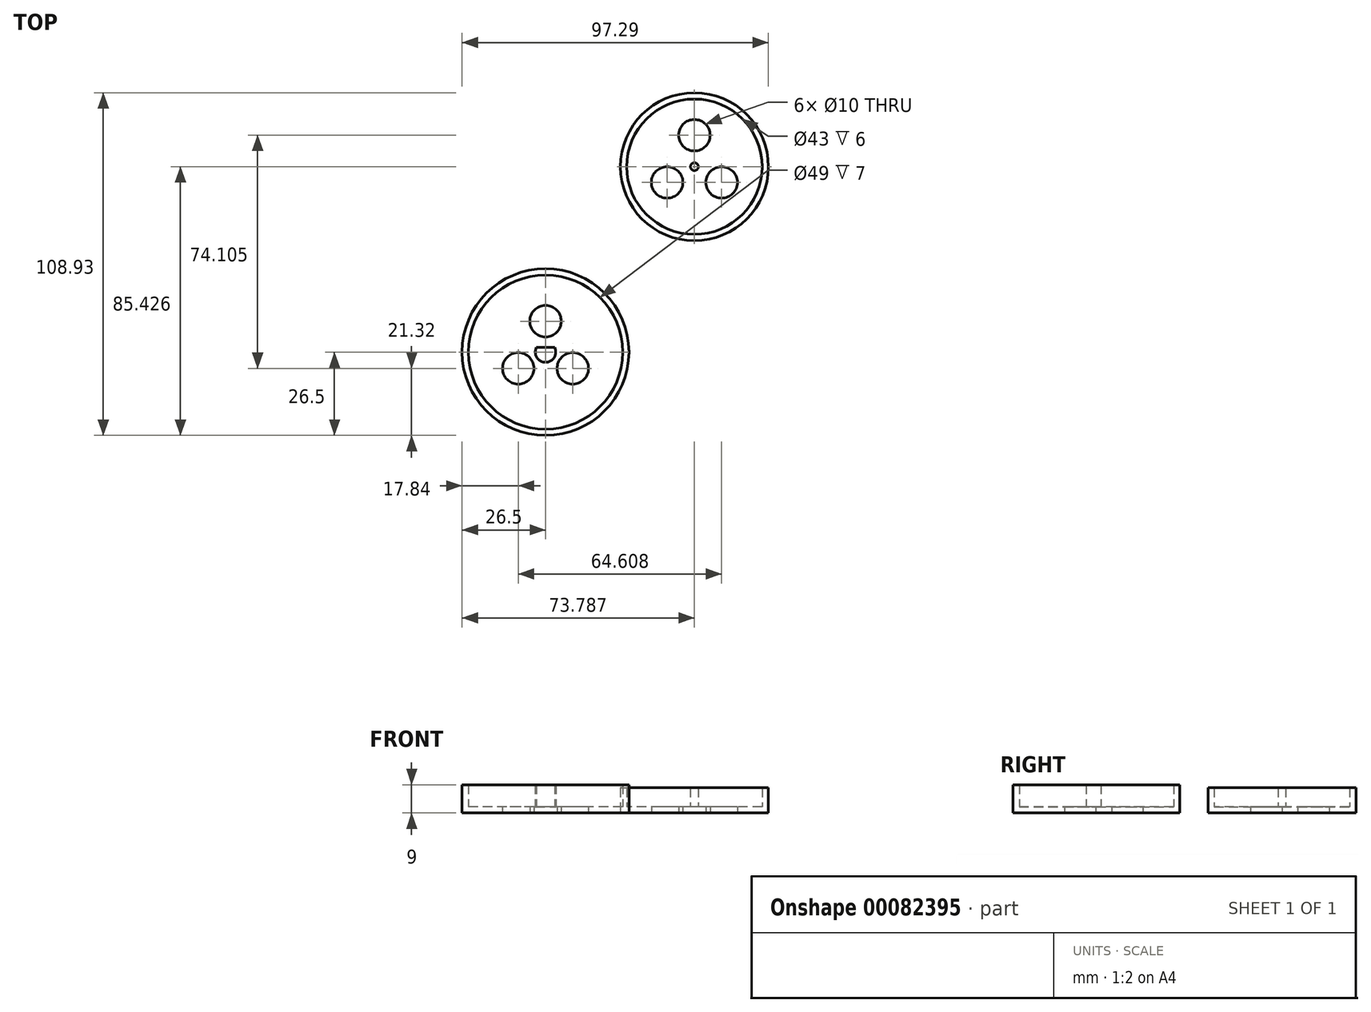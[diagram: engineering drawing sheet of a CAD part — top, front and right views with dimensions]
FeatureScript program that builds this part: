
annotation { "Feature Type Name" : "Feature", "Feature Type Description" : "" }
export const myFeature = defineFeature(function(context is Context, id is Id, definition is map)
    precondition{}
    {
        {
            var Q0;
            Q0=qCreatedBy(makeId("Top.planeOp"),FACE);
            var sketch = newSketch(context, id + "F0", { "sketchPlane" : qUnion([Q0])});
            skCircle(sketch, "E0", {"center": v(0, 0) * mm, "radius": 24.5 * mm});
            skCircle(sketch, "E1", {"center": v(0, 0) * mm, "radius": 26.5 * mm});
            skArc(sketch, "E2", {"start": v(-2.88, 1.5) * mm, "mid": v(0, -3.25) * mm, "end": v(2.88, 1.5) * mm});
            skLineSegment(sketch, "E3", {"start": v(2.88, 1.5) * mm, "end": v(-2.88, 1.5) * mm});
            skCircle(sketch, "E4", {"center": v(0, 9.82) * mm, "radius": 5 * mm});
            skCircle(sketch, "E5.1.0", {"center": v(-8.66, -5.18) * mm, "radius": 5 * mm});
            skCircle(sketch, "E5.2.0", {"center": v(8.66, -5.18) * mm, "radius": 5 * mm});
            skPoint(sketch, "E5.center", {"position": v(0, -0.18) * mm});
            skCircle(sketch, "E6", {"center": v(47.29, 58.93) * mm, "radius": 23.5 * mm});
            skCircle(sketch, "E7", {"center": v(47.29, 58.93) * mm, "radius": 21.5 * mm});
            skCircle(sketch, "E8", {"center": v(47.29, 68.93) * mm, "radius": 5 * mm});
            skCircle(sketch, "E9.1.0", {"center": v(38.63, 53.93) * mm, "radius": 5 * mm});
            skCircle(sketch, "E9.2.0", {"center": v(55.95, 53.93) * mm, "radius": 5 * mm});
            skCircle(sketch, "E10", {"center": v(47.29, 58.93) * mm, "radius": 1.25 * mm});
            skSolve(sketch);
        }
        {
            var Q0;
            Q0=makeQuery(id+"F0.imprint","IMPRINT",FACE,{"disambiguationData":[TD([[makeQuery(id+"F0.imprint","IMPRINT",EDGE,{"derivedFrom":sQuery(id+"F0.wireOp",EDGE,"E2")}),1.0]])]});
            var Q1;
            Q1=makeQuery(id+"F0.imprint","IMPRINT",FACE,{"disambiguationData":[TD([[makeQuery(id+"F0.imprint","IMPRINT",EDGE,{"derivedFrom":sQuery(id+"F0.wireOp",EDGE,"E0")}),-1.0]])]});
            extrude(context, id + "F1", {"entities" : qUnion([Q0, Q1]), "depth" : 9 * mm});
        }
        {
            var Q0;
            Q0=makeQuery(id+"F0.imprint","IMPRINT",FACE,{"disambiguationData":[TD([[makeQuery(id+"F0.imprint","IMPRINT",EDGE,{"derivedFrom":sQuery(id+"F0.wireOp",EDGE,"E0")}),1.0]])]});
            extrude(context, id + "F2", {"entities" : qUnion([Q0]), "operationType" : NewBodyOperationType.ADD, "depth" : 2 * mm});
        }
        {
            var Q0;
            Q0=makeQuery(id+"F1.opExtrude","SWEPT_BODY",BODY,{"disambiguationData":[OSD([sQuery(id+"F0.wireOp",EDGE,"E0"),sQuery(id+"F0.wireOp",EDGE,"E1")])]});
            transform(context, id + "F3", {"entities" : qUnion([Q0]), "transformType" : TransformType.TRANSLATION_3D, "dx" : 0 * mm, "dy" : 0 * mm, "dz" : 0 * mm, "makeCopy" : true});
        }
        {
            var Q0;
            Q0=makeQuery(id+"F1.opExtrude","SWEPT_BODY",BODY,{"disambiguationData":[OSD([sQuery(id+"F0.wireOp",EDGE,"E0"),sQuery(id+"F0.wireOp",EDGE,"E1")])]});
            deleteBodies(context, id + "F4", {"entities" : qUnion([Q0])});
        }
        {
            var Q0;
            Q0=makeQuery(id+"F0.imprint","IMPRINT",FACE,{"disambiguationData":[TD([[makeQuery(id+"F0.imprint","IMPRINT",EDGE,{"derivedFrom":sQuery(id+"F0.wireOp",EDGE,"E6")}),1.0]])]});
            var Q1;
            Q1=makeQuery(id+"F0.imprint","IMPRINT",FACE,{"disambiguationData":[TD([[makeQuery(id+"F0.imprint","IMPRINT",EDGE,{"derivedFrom":sQuery(id+"F0.wireOp",EDGE,"E10")}),1.0]])]});
            extrude(context, id + "F5", {"entities" : qUnion([Q0, Q1]), "operationType" : NewBodyOperationType.ADD, "depth" : 8 * mm});
        }
        {
            var Q0;
            Q0=makeQuery(id+"F0.imprint","IMPRINT",FACE,{"disambiguationData":[TD([[makeQuery(id+"F0.imprint","IMPRINT",EDGE,{"derivedFrom":sQuery(id+"F0.wireOp",EDGE,"E7")}),1.0]])]});
            extrude(context, id + "F6", {"entities" : qUnion([Q0]), "operationType" : NewBodyOperationType.ADD, "depth" : 2 * mm});
        }
    });
